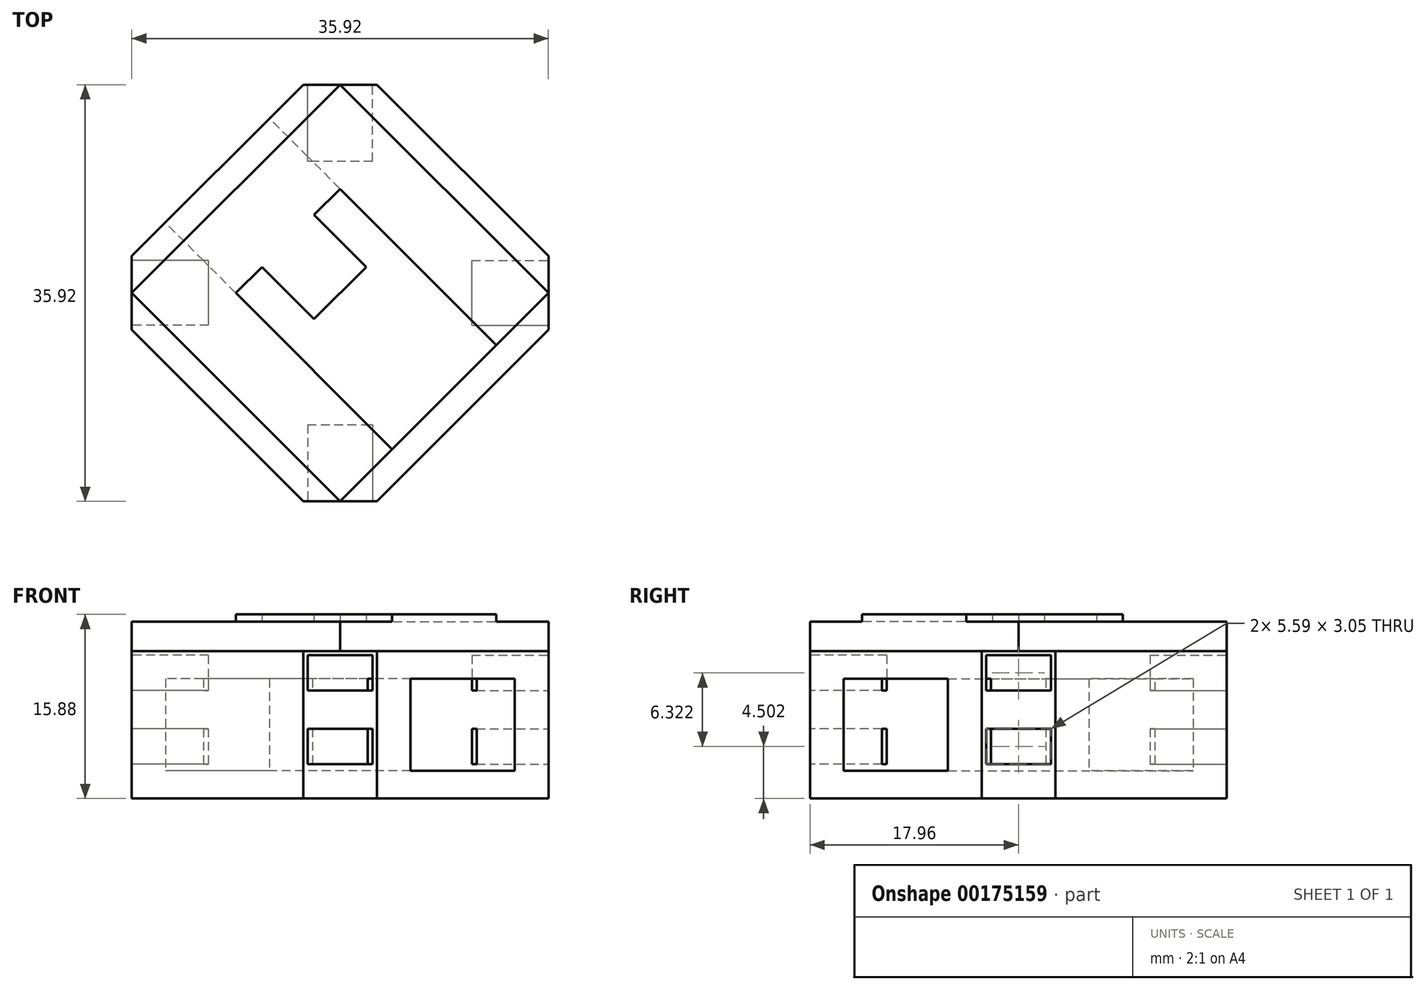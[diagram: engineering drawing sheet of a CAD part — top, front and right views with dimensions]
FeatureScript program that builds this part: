
annotation { "Feature Type Name" : "Feature", "Feature Type Description" : "" }
export const myFeature = defineFeature(function(context is Context, id is Id, definition is map)
    precondition{}
    {
        {
            var Q0;
            Q0=qCreatedBy(makeId("Top.planeOp"),FACE);
            var sketch = newSketch(context, id + "F0", { "sketchPlane" : qUnion([Q0])});
            skLineSegment(sketch, "E0.bottom", {"start": v(-17.96, 17.96) * mm, "end": v(17.96, 17.96) * mm});
            skLineSegment(sketch, "E0.top", {"start": v(-17.96, -17.96) * mm, "end": v(17.96, -17.96) * mm});
            skLineSegment(sketch, "E0.left", {"start": v(-17.96, 17.96) * mm, "end": v(-17.96, -17.96) * mm});
            skLineSegment(sketch, "E0.right", {"start": v(17.96, 17.96) * mm, "end": v(17.96, -17.96) * mm});
            skPoint(sketch, "E0.middle", {"position": v(0, 0) * mm});
            skPoint(sketch, "E1", {"position": v(-17.96, 3.17) * mm});
            skPoint(sketch, "E2", {"position": v(-17.96, -3.18) * mm});
            skPoint(sketch, "E3", {"position": v(-17.96, 0) * mm});
            skPoint(sketch, "E4", {"position": v(0, 17.96) * mm});
            skPoint(sketch, "E5", {"position": v(-3.17, 17.96) * mm});
            skPoint(sketch, "E6", {"position": v(3.18, 17.96) * mm});
            skPoint(sketch, "E7", {"position": v(17.96, 0) * mm});
            skPoint(sketch, "E8", {"position": v(17.96, 3.17) * mm});
            skPoint(sketch, "E9", {"position": v(17.96, -3.18) * mm});
            skPoint(sketch, "E10", {"position": v(0, -17.96) * mm});
            skPoint(sketch, "E11", {"position": v(3.18, -17.96) * mm});
            skPoint(sketch, "E12", {"position": v(-3.17, -17.96) * mm});
            skLineSegment(sketch, "E13", {"start": v(-17.96, 3.17) * mm, "end": v(-3.17, 17.96) * mm});
            skLineSegment(sketch, "E14", {"start": v(3.18, 17.96) * mm, "end": v(17.96, 3.17) * mm});
            skLineSegment(sketch, "E15", {"start": v(17.96, -3.18) * mm, "end": v(3.18, -17.96) * mm});
            skLineSegment(sketch, "E16", {"start": v(-17.96, -3.18) * mm, "end": v(-3.17, -17.96) * mm});
            skLineSegment(sketch, "E17", {"start": v(0, 0) * mm, "end": v(-8.98, 8.98) * mm});
            skLineSegment(sketch, "E18", {"start": v(0, 0) * mm, "end": v(8.98, 8.98) * mm});
            skLineSegment(sketch, "E19", {"start": v(0, 0) * mm, "end": v(8.98, -8.98) * mm});
            skLineSegment(sketch, "E20", {"start": v(0, 0) * mm, "end": v(-8.98, -8.98) * mm});
            skLineSegment(sketch, "E21", {"start": v(-8.98, -8.98) * mm, "end": v(0, -17.96) * mm});
            skLineSegment(sketch, "E22", {"start": v(0, -17.96) * mm, "end": v(8.98, -8.98) * mm});
            skLineSegment(sketch, "E23", {"start": v(-8.98, 8.98) * mm, "end": v(-17.96, 0) * mm});
            skLineSegment(sketch, "E24", {"start": v(-17.96, 0) * mm, "end": v(-8.98, -8.98) * mm});
            skLineSegment(sketch, "E25", {"start": v(-8.98, 8.98) * mm, "end": v(0, 17.96) * mm});
            skLineSegment(sketch, "E26", {"start": v(0, 17.96) * mm, "end": v(8.98, 8.98) * mm});
            skLineSegment(sketch, "E27", {"start": v(8.98, 8.98) * mm, "end": v(17.96, 0) * mm});
            skLineSegment(sketch, "E28", {"start": v(17.96, 0) * mm, "end": v(8.98, -8.98) * mm});
            skSolve(sketch);
        }
        {
            var Q0;
            Q0=makeQuery(id+"F0.imprint","IMPRINT",FACE,{"disambiguationData":[TD([[makeQuery(id+"F0.imprint","IMPRINT",EDGE,{"derivedFrom":sQuery(id+"F0.wireOp",EDGE,"E17")}),-1.0]])]});
            var Q1;
            Q1=makeQuery(id+"F0.imprint","IMPRINT",FACE,{"disambiguationData":[TD([[makeQuery(id+"F0.imprint","IMPRINT",EDGE,{"derivedFrom":sQuery(id+"F0.wireOp",EDGE,"E18")}),-1.0]])]});
            var Q2;
            Q2=makeQuery(id+"F0.imprint","IMPRINT",FACE,{"disambiguationData":[TD([[makeQuery(id+"F0.imprint","IMPRINT",EDGE,{"derivedFrom":sQuery(id+"F0.wireOp",EDGE,"E19")}),-1.0]])]});
            var Q3;
            Q3=makeQuery(id+"F0.imprint","IMPRINT",FACE,{"disambiguationData":[TD([[makeQuery(id+"F0.imprint","IMPRINT",EDGE,{"derivedFrom":sQuery(id+"F0.wireOp",EDGE,"E17")}),1.0]])]});
            extrude(context, id + "F1", {"entities" : qUnion([Q0, Q1, Q2, Q3]), "depth" : 15.24 * mm});
        }
        {
            var Q0;
            {var subQ1=sQuery(id+"F0.wireOp",EDGE,"E13");Q0=makeQuery(id+"F0.imprint","IMPRINT",FACE,{"disambiguationData":[TD([[makeQuery(id+"F0.imprint","IMPRINT",EDGE,{"derivedFrom":subQ1}),-1.0]])]});}
            var Q1;
            {var subQ1=sQuery(id+"F0.wireOp",EDGE,"E16");Q1=makeQuery(id+"F0.imprint","IMPRINT",FACE,{"disambiguationData":[TD([[makeQuery(id+"F0.imprint","IMPRINT",EDGE,{"derivedFrom":subQ1}),1.0]])]});}
            var Q2;
            {var subQ1=sQuery(id+"F0.wireOp",EDGE,"E15");Q2=makeQuery(id+"F0.imprint","IMPRINT",FACE,{"disambiguationData":[TD([[makeQuery(id+"F0.imprint","IMPRINT",EDGE,{"derivedFrom":subQ1}),-1.0]])]});}
            var Q3;
            {var subQ1=sQuery(id+"F0.wireOp",EDGE,"E14");Q3=makeQuery(id+"F0.imprint","IMPRINT",FACE,{"disambiguationData":[TD([[makeQuery(id+"F0.imprint","IMPRINT",EDGE,{"derivedFrom":subQ1}),-1.0]])]});}
            extrude(context, id + "F2", {"entities" : qUnion([Q0, Q1, Q2, Q3]), "operationType" : NewBodyOperationType.ADD, "depth" : 12.7 * mm});
        }
        {
            var Q0;
            Q0=makeQuery(id+"F2.opExtrude","CAP_FACE",FACE,{"disambiguationData":[OSD([sQuery(id+"F0.wireOp",EDGE,"E21"),sQuery(id+"F0.wireOp",EDGE,"E22"),sQuery(id+"F0.wireOp",EDGE,"E23"),sQuery(id+"F0.wireOp",EDGE,"E24"),sQuery(id+"F0.wireOp",EDGE,"E25"),sQuery(id+"F0.wireOp",EDGE,"E26"),sQuery(id+"F0.wireOp",EDGE,"E27"),sQuery(id+"F0.wireOp",EDGE,"E28")])],"isStart":false});
            var sketch = newSketch(context, id + "F3", { "sketchPlane" : qUnion([Q0])});
            skPoint(sketch, "E29", {"position": v(8.98, -8.98) * mm});
            skLineSegment(sketch, "E30", {"start": v(8.98, -8.98) * mm, "end": v(13.47, -4.5) * mm});
            skLineSegment(sketch, "E31", {"start": v(13.47, -4.5) * mm, "end": v(0, 8.98) * mm});
            skLineSegment(sketch, "E32", {"start": v(0, 8.98) * mm, "end": v(-2.25, 6.74) * mm});
            skLineSegment(sketch, "E33", {"start": v(-2.25, 6.74) * mm, "end": v(2.25, 2.25) * mm});
            skLineSegment(sketch, "E34", {"start": v(8.98, -8.98) * mm, "end": v(0, 0) * mm});
            skLineSegment(sketch, "E35", {"start": v(0, 0) * mm, "end": v(2.25, 2.25) * mm});
            skLineSegment(sketch, "E36.MirrorCS", {"start": v(0, 0) * mm, "end": v(-2.25, -2.25) * mm});
            skLineSegment(sketch, "E37.MirrorCS", {"start": v(-6.74, 2.25) * mm, "end": v(-2.25, -2.25) * mm});
            skLineSegment(sketch, "E38.MirrorCS", {"start": v(-8.98, 0) * mm, "end": v(-6.74, 2.25) * mm});
            skLineSegment(sketch, "E39.MirrorCS", {"start": v(4.5, -13.47) * mm, "end": v(-8.98, 0) * mm});
            skLineSegment(sketch, "E40.MirrorCS", {"start": v(8.98, -8.98) * mm, "end": v(4.5, -13.47) * mm});
            skSolve(sketch);
        }
        {
            var Q0;
            {var subQ0=sQuery(id+"F0.wireOp",EDGE,"E0.left");Q0=makeQuery(id+"F2.boolean.opBoolean","MERGE",FACE,{"derivedFrom":[makeQuery(id+"F2.opExtrude","SWEPT_FACE",FACE,{"disambiguationData":[OSD([subQ0]),TDD([makeQuery(id+"F0.imprint","IMPRINT",EDGE,{"disambiguationData":[TD([[makeQuery(id+"F0.imprint","INTERSECT",VERTEX,{"derivedFrom":[subQ0,sQuery(id+"F0.wireOp",EDGE,"E13")]}),-1.0]])],"derivedFrom":subQ0})])]}),makeQuery(id+"F2.opExtrude","SWEPT_FACE",FACE,{"disambiguationData":[OSD([subQ0]),TDD([makeQuery(id+"F0.imprint","IMPRINT",EDGE,{"disambiguationData":[TD([[makeQuery(id+"F0.imprint","INTERSECT",VERTEX,{"derivedFrom":[subQ0,sQuery(id+"F0.wireOp",EDGE,"E16")]}),1.0]])],"derivedFrom":subQ0})])]})]});}
            var sketch = newSketch(context, id + "F4", { "sketchPlane" : qUnion([Q0])});
            skPoint(sketch, "E41", {"position": v(0, 7.62) * mm});
            skPoint(sketch, "E42.positionSnap0", {"position": v(0, 5.33) * mm});
            skPoint(sketch, "E42.positionSnap1", {"position": v(3.3, 7.62) * mm});
            skLineSegment(sketch, "E43.bottom", {"start": v(-2.54, 12.07) * mm, "end": v(2.54, 12.07) * mm});
            skLineSegment(sketch, "E43.top", {"start": v(-2.54, 3.17) * mm, "end": v(2.54, 3.17) * mm});
            skLineSegment(sketch, "E44", {"start": v(-2.54, 9.58) * mm, "end": v(2.54, 9.58) * mm});
            skLineSegment(sketch, "E45", {"start": v(-2.54, 5.83) * mm, "end": v(2.54, 5.83) * mm});
            skLineSegment(sketch, "E46", {"start": v(-2.54, 12.07) * mm, "end": v(-2.54, 9.58) * mm});
            skLineSegment(sketch, "E47", {"start": v(2.54, 12.07) * mm, "end": v(2.54, 9.58) * mm});
            skLineSegment(sketch, "E48", {"start": v(-2.54, 5.83) * mm, "end": v(-2.54, 3.17) * mm});
            skLineSegment(sketch, "E49", {"start": v(2.54, 5.83) * mm, "end": v(2.54, 3.17) * mm});
            skPoint(sketch, "E50", {"position": v(0, 10.82) * mm});
            skPoint(sketch, "E50.positionSnap0", {"position": v(-2.54, 10.82) * mm});
            skPoint(sketch, "E50.positionSnap1", {"position": v(0, 9.58) * mm});
            skPoint(sketch, "E51", {"position": v(0, 4.5) * mm});
            skPoint(sketch, "E51.positionSnap0", {"position": v(-2.54, 4.5) * mm});
            skPoint(sketch, "E51.positionSnap1", {"position": v(0, 3.17) * mm});
            skLineSegment(sketch, "E52.bottom", {"start": v(-2.8, 6.03) * mm, "end": v(2.8, 6.03) * mm});
            skLineSegment(sketch, "E52.top", {"start": v(-2.8, 2.98) * mm, "end": v(2.8, 2.98) * mm});
            skLineSegment(sketch, "E52.left", {"start": v(-2.8, 6.03) * mm, "end": v(-2.8, 2.98) * mm});
            skLineSegment(sketch, "E52.right", {"start": v(2.8, 6.03) * mm, "end": v(2.8, 2.98) * mm});
            skLineSegment(sketch, "E53.bottom", {"start": v(-2.8, 12.35) * mm, "end": v(2.8, 12.35) * mm});
            skLineSegment(sketch, "E53.top", {"start": v(-2.8, 9.3) * mm, "end": v(2.8, 9.3) * mm});
            skLineSegment(sketch, "E53.left", {"start": v(-2.8, 12.35) * mm, "end": v(-2.8, 9.3) * mm});
            skLineSegment(sketch, "E53.right", {"start": v(2.8, 12.35) * mm, "end": v(2.8, 9.3) * mm});
            skLineSegment(sketch, "E54", {"start": v(0, 7.62) * mm, "end": v(0, 0) * mm});
            skSolve(sketch);
        }
        {
            var Q0;
            Q0=makeQuery(id+"F4.imprint","IMPRINT",FACE,{"disambiguationData":[TD([[makeQuery(id+"F4.imprint","IMPRINT",EDGE,{"derivedFrom":sQuery(id+"F4.wireOp",EDGE,"E43.bottom")}),1.0]])]});
            var Q1;
            Q1=makeQuery(id+"F4.imprint","IMPRINT",FACE,{"disambiguationData":[TD([[makeQuery(id+"F4.imprint","IMPRINT",EDGE,{"derivedFrom":sQuery(id+"F4.wireOp",EDGE,"E43.bottom")}),-1.0]])]});
            var Q2;
            Q2=makeQuery(id+"F4.imprint","IMPRINT",FACE,{"disambiguationData":[TD([[makeQuery(id+"F4.imprint","IMPRINT",EDGE,{"derivedFrom":sQuery(id+"F4.wireOp",EDGE,"E43.top")}),1.0]])]});
            var Q3;
            {var subQ4=sQuery(id+"F4.wireOp",EDGE,"E48");Q3=makeQuery(id+"F4.imprint","IMPRINT",FACE,{"disambiguationData":[TD([[makeQuery(id+"F4.imprint","IMPRINT",EDGE,{"derivedFrom":subQ4}),-1.0]])]});}
            var Q4;
            {var subQ8=sQuery(id+"F4.wireOp",EDGE,"E49");Q4=makeQuery(id+"F4.imprint","IMPRINT",FACE,{"disambiguationData":[TD([[makeQuery(id+"F4.imprint","IMPRINT",EDGE,{"derivedFrom":subQ8}),1.0]])]});}
            extrude(context, id + "F5", {"entities" : qUnion([Q0, Q1, Q2, Q3, Q4]), "operationType" : NewBodyOperationType.REMOVE, "oppositeDirection" : true, "depth" : 6.6 * mm});
        }
        {
            var Q0;
            {var subQ0=sQuery(id+"F0.wireOp",EDGE,"E0.right");Q0=makeQuery(id+"F2.boolean.opBoolean","MERGE",FACE,{"derivedFrom":[makeQuery(id+"F2.opExtrude","SWEPT_FACE",FACE,{"disambiguationData":[OSD([subQ0]),TDD([makeQuery(id+"F0.imprint","IMPRINT",EDGE,{"disambiguationData":[TD([[makeQuery(id+"F0.imprint","INTERSECT",VERTEX,{"derivedFrom":[subQ0,sQuery(id+"F0.wireOp",EDGE,"E14")]}),-1.0]])],"derivedFrom":subQ0})])]}),makeQuery(id+"F2.opExtrude","SWEPT_FACE",FACE,{"disambiguationData":[OSD([subQ0]),TDD([makeQuery(id+"F0.imprint","IMPRINT",EDGE,{"disambiguationData":[TD([[makeQuery(id+"F0.imprint","INTERSECT",VERTEX,{"derivedFrom":[subQ0,sQuery(id+"F0.wireOp",EDGE,"E15")]}),1.0]])],"derivedFrom":subQ0})])]})]});}
            var sketch = newSketch(context, id + "F6", { "sketchPlane" : qUnion([Q0])});
            skPoint(sketch, "E55", {"position": v(0, 7.62) * mm});
            skPoint(sketch, "E56.positionSnap0", {"position": v(0, 4.31) * mm});
            skPoint(sketch, "E56.positionSnap1", {"position": v(3.3, 7.62) * mm});
            skLineSegment(sketch, "E57.bottom", {"start": v(-2.54, 12.07) * mm, "end": v(2.54, 12.07) * mm});
            skLineSegment(sketch, "E57.top", {"start": v(-2.54, 3.18) * mm, "end": v(2.54, 3.18) * mm});
            skLineSegment(sketch, "E58", {"start": v(-2.54, 9.58) * mm, "end": v(2.54, 9.58) * mm});
            skLineSegment(sketch, "E59", {"start": v(-2.54, 5.83) * mm, "end": v(2.54, 5.83) * mm});
            skLineSegment(sketch, "E60", {"start": v(-2.54, 12.07) * mm, "end": v(-2.54, 9.58) * mm});
            skLineSegment(sketch, "E61", {"start": v(2.54, 12.07) * mm, "end": v(2.54, 9.58) * mm});
            skLineSegment(sketch, "E62", {"start": v(-2.54, 5.83) * mm, "end": v(-2.54, 3.18) * mm});
            skLineSegment(sketch, "E63", {"start": v(2.54, 5.83) * mm, "end": v(2.54, 3.18) * mm});
            skPoint(sketch, "E64", {"position": v(0, 10.82) * mm});
            skPoint(sketch, "E64.positionSnap0", {"position": v(-2.54, 10.82) * mm});
            skPoint(sketch, "E64.positionSnap1", {"position": v(0, 9.58) * mm});
            skPoint(sketch, "E65", {"position": v(0, 4.5) * mm});
            skPoint(sketch, "E65.positionSnap0", {"position": v(-2.54, 4.5) * mm});
            skPoint(sketch, "E65.positionSnap1", {"position": v(0, 3.18) * mm});
            skLineSegment(sketch, "E66.bottom", {"start": v(-2.8, 6.03) * mm, "end": v(2.8, 6.03) * mm});
            skLineSegment(sketch, "E66.top", {"start": v(-2.8, 2.98) * mm, "end": v(2.8, 2.98) * mm});
            skLineSegment(sketch, "E66.left", {"start": v(-2.8, 6.03) * mm, "end": v(-2.8, 2.98) * mm});
            skLineSegment(sketch, "E66.right", {"start": v(2.8, 6.03) * mm, "end": v(2.8, 2.98) * mm});
            skLineSegment(sketch, "E67.bottom", {"start": v(-2.8, 12.35) * mm, "end": v(2.8, 12.35) * mm});
            skLineSegment(sketch, "E67.top", {"start": v(-2.8, 9.3) * mm, "end": v(2.8, 9.3) * mm});
            skLineSegment(sketch, "E67.left", {"start": v(-2.8, 12.35) * mm, "end": v(-2.8, 9.3) * mm});
            skLineSegment(sketch, "E67.right", {"start": v(2.8, 12.35) * mm, "end": v(2.8, 9.3) * mm});
            skLineSegment(sketch, "E68", {"start": v(0, 7.62) * mm, "end": v(0, 0) * mm});
            skSolve(sketch);
        }
        {
            var Q0;
            Q0=makeQuery(id+"F6.imprint","IMPRINT",FACE,{"disambiguationData":[TD([[makeQuery(id+"F6.imprint","IMPRINT",EDGE,{"derivedFrom":sQuery(id+"F6.wireOp",EDGE,"E57.bottom")}),-1.0]])]});
            var Q1;
            {var subQ0=sQuery(id+"F6.wireOp",EDGE,"E63");Q1=makeQuery(id+"F6.imprint","IMPRINT",FACE,{"disambiguationData":[TD([[makeQuery(id+"F6.imprint","IMPRINT",EDGE,{"derivedFrom":subQ0}),-1.0]])]});}
            var Q2;
            {var subQ0=sQuery(id+"F6.wireOp",EDGE,"E62");Q2=makeQuery(id+"F6.imprint","IMPRINT",FACE,{"disambiguationData":[TD([[makeQuery(id+"F6.imprint","IMPRINT",EDGE,{"derivedFrom":subQ0}),1.0]])]});}
            var Q3;
            {var subQ4=sQuery(id+"F6.wireOp",EDGE,"E62");Q3=makeQuery(id+"F6.imprint","IMPRINT",FACE,{"disambiguationData":[TD([[makeQuery(id+"F6.imprint","IMPRINT",EDGE,{"derivedFrom":subQ4}),-1.0]])]});}
            var Q4;
            {var subQ4=sQuery(id+"F6.wireOp",EDGE,"E63");Q4=makeQuery(id+"F6.imprint","IMPRINT",FACE,{"disambiguationData":[TD([[makeQuery(id+"F6.imprint","IMPRINT",EDGE,{"derivedFrom":subQ4}),1.0]])]});}
            var Q5;
            Q5=makeQuery(id+"F6.imprint","IMPRINT",FACE,{"disambiguationData":[TD([[makeQuery(id+"F6.imprint","IMPRINT",EDGE,{"derivedFrom":sQuery(id+"F6.wireOp",EDGE,"E57.bottom")}),1.0]])]});
            extrude(context, id + "F7", {"entities" : qUnion([Q0, Q1, Q2, Q3, Q4, Q5]), "operationType" : NewBodyOperationType.REMOVE, "oppositeDirection" : true, "depth" : 6.6 * mm});
        }
        {
            var Q0;
            {var subQ0=sQuery(id+"F0.wireOp",EDGE,"E0.top");Q0=makeQuery(id+"F2.boolean.opBoolean","MERGE",FACE,{"derivedFrom":[makeQuery(id+"F2.opExtrude","SWEPT_FACE",FACE,{"disambiguationData":[OSD([subQ0]),TDD([makeQuery(id+"F0.imprint","IMPRINT",EDGE,{"disambiguationData":[TD([[makeQuery(id+"F0.imprint","INTERSECT",VERTEX,{"derivedFrom":[subQ0,sQuery(id+"F0.wireOp",EDGE,"E16")]}),-1.0]])],"derivedFrom":subQ0})])]}),makeQuery(id+"F2.opExtrude","SWEPT_FACE",FACE,{"disambiguationData":[OSD([subQ0]),TDD([makeQuery(id+"F0.imprint","IMPRINT",EDGE,{"disambiguationData":[TD([[makeQuery(id+"F0.imprint","INTERSECT",VERTEX,{"derivedFrom":[subQ0,sQuery(id+"F0.wireOp",EDGE,"E15")]}),1.0]])],"derivedFrom":subQ0})])]})]});}
            var sketch = newSketch(context, id + "F8", { "sketchPlane" : qUnion([Q0])});
            skPoint(sketch, "E69", {"position": v(0, 7.62) * mm});
            skPoint(sketch, "E69.positionSnap0", {"position": v(-25.4, 7.62) * mm});
            skPoint(sketch, "E70.positionSnap0", {"position": v(0, 5.76) * mm});
            skPoint(sketch, "E70.positionSnap1", {"position": v(3.3, 7.62) * mm});
            skLineSegment(sketch, "E71.bottom", {"start": v(-2.54, 12.07) * mm, "end": v(2.54, 12.07) * mm});
            skLineSegment(sketch, "E71.top", {"start": v(-2.54, 3.17) * mm, "end": v(2.54, 3.17) * mm});
            skLineSegment(sketch, "E72", {"start": v(-2.54, 9.58) * mm, "end": v(2.54, 9.58) * mm});
            skLineSegment(sketch, "E73", {"start": v(-2.54, 5.83) * mm, "end": v(2.54, 5.83) * mm});
            skLineSegment(sketch, "E74", {"start": v(-2.54, 12.07) * mm, "end": v(-2.54, 9.58) * mm});
            skLineSegment(sketch, "E75", {"start": v(2.54, 12.07) * mm, "end": v(2.54, 9.58) * mm});
            skLineSegment(sketch, "E76", {"start": v(-2.54, 5.83) * mm, "end": v(-2.54, 3.17) * mm});
            skLineSegment(sketch, "E77", {"start": v(2.54, 5.83) * mm, "end": v(2.54, 3.17) * mm});
            skPoint(sketch, "E78", {"position": v(0, 10.82) * mm});
            skPoint(sketch, "E78.positionSnap0", {"position": v(-2.54, 10.82) * mm});
            skPoint(sketch, "E78.positionSnap1", {"position": v(0, 9.58) * mm});
            skPoint(sketch, "E79", {"position": v(0, 4.5) * mm});
            skPoint(sketch, "E79.positionSnap0", {"position": v(-2.54, 4.5) * mm});
            skPoint(sketch, "E79.positionSnap1", {"position": v(0, 3.17) * mm});
            skLineSegment(sketch, "E80.bottom", {"start": v(-2.8, 6.03) * mm, "end": v(2.8, 6.03) * mm});
            skLineSegment(sketch, "E80.top", {"start": v(-2.8, 2.98) * mm, "end": v(2.8, 2.98) * mm});
            skLineSegment(sketch, "E80.left", {"start": v(-2.8, 6.03) * mm, "end": v(-2.8, 2.98) * mm});
            skLineSegment(sketch, "E80.right", {"start": v(2.8, 6.03) * mm, "end": v(2.8, 2.98) * mm});
            skLineSegment(sketch, "E81.bottom", {"start": v(-2.8, 12.35) * mm, "end": v(2.8, 12.35) * mm});
            skLineSegment(sketch, "E81.top", {"start": v(-2.8, 9.3) * mm, "end": v(2.8, 9.3) * mm});
            skLineSegment(sketch, "E81.left", {"start": v(-2.8, 12.35) * mm, "end": v(-2.8, 9.3) * mm});
            skLineSegment(sketch, "E81.right", {"start": v(2.8, 12.35) * mm, "end": v(2.8, 9.3) * mm});
            skLineSegment(sketch, "E82", {"start": v(0, 7.62) * mm, "end": v(0, 0) * mm});
            skSolve(sketch);
        }
        {
            var Q0;
            Q0=makeQuery(id+"F8.imprint","IMPRINT",FACE,{"disambiguationData":[TD([[makeQuery(id+"F8.imprint","IMPRINT",EDGE,{"derivedFrom":sQuery(id+"F8.wireOp",EDGE,"E71.bottom")}),1.0]])]});
            var Q1;
            {var subQ4=sQuery(id+"F8.wireOp",EDGE,"E77");Q1=makeQuery(id+"F8.imprint","IMPRINT",FACE,{"disambiguationData":[TD([[makeQuery(id+"F8.imprint","IMPRINT",EDGE,{"derivedFrom":subQ4}),1.0]])]});}
            var Q2;
            {var subQ4=sQuery(id+"F8.wireOp",EDGE,"E76");Q2=makeQuery(id+"F8.imprint","IMPRINT",FACE,{"disambiguationData":[TD([[makeQuery(id+"F8.imprint","IMPRINT",EDGE,{"derivedFrom":subQ4}),-1.0]])]});}
            var Q3;
            {var subQ0=sQuery(id+"F8.wireOp",EDGE,"E76");Q3=makeQuery(id+"F8.imprint","IMPRINT",FACE,{"disambiguationData":[TD([[makeQuery(id+"F8.imprint","IMPRINT",EDGE,{"derivedFrom":subQ0}),1.0]])]});}
            var Q4;
            Q4=makeQuery(id+"F8.imprint","IMPRINT",FACE,{"disambiguationData":[TD([[makeQuery(id+"F8.imprint","IMPRINT",EDGE,{"derivedFrom":sQuery(id+"F8.wireOp",EDGE,"E71.bottom")}),-1.0]])]});
            var Q5;
            {var subQ0=sQuery(id+"F8.wireOp",EDGE,"E77");Q5=makeQuery(id+"F8.imprint","IMPRINT",FACE,{"disambiguationData":[TD([[makeQuery(id+"F8.imprint","IMPRINT",EDGE,{"derivedFrom":subQ0}),-1.0]])]});}
            extrude(context, id + "F9", {"entities" : qUnion([Q0, Q1, Q2, Q3, Q4, Q5]), "operationType" : NewBodyOperationType.REMOVE, "oppositeDirection" : true, "depth" : 6.6 * mm});
        }
        {
            var Q0;
            Q0 = qSketchRegion(id + "F3", true);
            extrude(context, id + "F10", {"entities" : qUnion([Q0]), "operationType" : NewBodyOperationType.ADD, "depth" : 3.17 * mm});
        }
        {
            var Q0;
            {var subQ0=sQuery(id+"F0.wireOp",EDGE,"E0.bottom");Q0=makeQuery(id+"F2.boolean.opBoolean","MERGE",FACE,{"derivedFrom":[makeQuery(id+"F2.opExtrude","SWEPT_FACE",FACE,{"disambiguationData":[OSD([subQ0]),TDD([makeQuery(id+"F0.imprint","IMPRINT",EDGE,{"disambiguationData":[TD([[makeQuery(id+"F0.imprint","INTERSECT",VERTEX,{"derivedFrom":[subQ0,sQuery(id+"F0.wireOp",EDGE,"E13")]}),-1.0]])],"derivedFrom":subQ0})])]}),makeQuery(id+"F2.opExtrude","SWEPT_FACE",FACE,{"disambiguationData":[OSD([subQ0]),TDD([makeQuery(id+"F0.imprint","IMPRINT",EDGE,{"disambiguationData":[TD([[makeQuery(id+"F0.imprint","INTERSECT",VERTEX,{"derivedFrom":[subQ0,sQuery(id+"F0.wireOp",EDGE,"E14")]}),1.0]])],"derivedFrom":subQ0})])]})]});}
            var sketch = newSketch(context, id + "F11", { "sketchPlane" : qUnion([Q0])});
            skPoint(sketch, "E83", {"position": v(0, 7.62) * mm});
            skPoint(sketch, "E84.positionSnap0", {"position": v(0, 4.31) * mm});
            skPoint(sketch, "E84.positionSnap1", {"position": v(3.3, 7.62) * mm});
            skLineSegment(sketch, "E85.bottom", {"start": v(-2.54, 12.07) * mm, "end": v(2.54, 12.07) * mm});
            skLineSegment(sketch, "E85.top", {"start": v(-2.54, 3.18) * mm, "end": v(2.54, 3.18) * mm});
            skLineSegment(sketch, "E86", {"start": v(-2.54, 9.58) * mm, "end": v(2.54, 9.58) * mm});
            skLineSegment(sketch, "E87", {"start": v(-2.54, 5.83) * mm, "end": v(2.54, 5.83) * mm});
            skLineSegment(sketch, "E88", {"start": v(-2.54, 12.07) * mm, "end": v(-2.54, 9.58) * mm});
            skLineSegment(sketch, "E89", {"start": v(2.54, 12.07) * mm, "end": v(2.54, 9.58) * mm});
            skLineSegment(sketch, "E90", {"start": v(-2.54, 5.83) * mm, "end": v(-2.54, 3.18) * mm});
            skLineSegment(sketch, "E91", {"start": v(2.54, 5.83) * mm, "end": v(2.54, 3.18) * mm});
            skPoint(sketch, "E92", {"position": v(0, 10.82) * mm});
            skPoint(sketch, "E92.positionSnap0", {"position": v(-2.54, 10.82) * mm});
            skPoint(sketch, "E92.positionSnap1", {"position": v(0, 9.58) * mm});
            skPoint(sketch, "E93", {"position": v(0, 4.5) * mm});
            skPoint(sketch, "E93.positionSnap0", {"position": v(-2.54, 4.5) * mm});
            skPoint(sketch, "E93.positionSnap1", {"position": v(0, 3.18) * mm});
            skLineSegment(sketch, "E94.bottom", {"start": v(-2.8, 6.03) * mm, "end": v(2.8, 6.03) * mm});
            skLineSegment(sketch, "E94.top", {"start": v(-2.8, 2.98) * mm, "end": v(2.8, 2.98) * mm});
            skLineSegment(sketch, "E94.left", {"start": v(-2.8, 6.03) * mm, "end": v(-2.8, 2.98) * mm});
            skLineSegment(sketch, "E94.right", {"start": v(2.8, 6.03) * mm, "end": v(2.8, 2.98) * mm});
            skLineSegment(sketch, "E95.bottom", {"start": v(-2.8, 12.35) * mm, "end": v(2.8, 12.35) * mm});
            skLineSegment(sketch, "E95.top", {"start": v(-2.8, 9.3) * mm, "end": v(2.8, 9.3) * mm});
            skLineSegment(sketch, "E95.left", {"start": v(-2.8, 12.35) * mm, "end": v(-2.8, 9.3) * mm});
            skLineSegment(sketch, "E95.right", {"start": v(2.8, 12.35) * mm, "end": v(2.8, 9.3) * mm});
            skLineSegment(sketch, "E96", {"start": v(0, 7.62) * mm, "end": v(0, 0) * mm});
            skSolve(sketch);
        }
        {
            var Q0;
            Q0 = qSketchRegion(id + "F11", true);
            var Q1;
            {var subQ0=sQuery(id+"F11.wireOp",EDGE,"E90");Q1=makeQuery(id+"F11.imprint","IMPRINT",FACE,{"disambiguationData":[TD([[makeQuery(id+"F11.imprint","IMPRINT",EDGE,{"derivedFrom":subQ0}),1.0]])]});}
            var Q2;
            {var subQ0=sQuery(id+"F11.wireOp",EDGE,"E91");Q2=makeQuery(id+"F11.imprint","IMPRINT",FACE,{"disambiguationData":[TD([[makeQuery(id+"F11.imprint","IMPRINT",EDGE,{"derivedFrom":subQ0}),-1.0]])]});}
            var Q3;
            Q3=makeQuery(id+"F11.imprint","IMPRINT",FACE,{"disambiguationData":[TD([[makeQuery(id+"F11.imprint","IMPRINT",EDGE,{"derivedFrom":sQuery(id+"F11.wireOp",EDGE,"E85.bottom")}),-1.0]])]});
            extrude(context, id + "F12", {"entities" : qUnion([Q0, Q1, Q2, Q3]), "operationType" : NewBodyOperationType.REMOVE, "oppositeDirection" : true, "depth" : 6.6 * mm});
        }
        {
            var Q0;
            Q0=makeQuery(id+"F2.opExtrude","SWEPT_FACE",FACE,{"disambiguationData":[OSD([sQuery(id+"F0.wireOp",EDGE,"E13")])]});
            var sketch = newSketch(context, id + "F13", { "sketchPlane" : qUnion([Q0])});
            skLineSegment(sketch, "E97", {"start": v(0, 0) * mm, "end": v(0, 6.35) * mm});
            skPoint(sketch, "E97.endSnap0", {"position": v(0, 12.7) * mm});
            skLineSegment(sketch, "E98.bottom", {"start": v(-6.35, 10.32) * mm, "end": v(6.35, 10.32) * mm});
            skLineSegment(sketch, "E98.top", {"start": v(-6.35, 2.38) * mm, "end": v(6.35, 2.38) * mm});
            skLineSegment(sketch, "E98.left", {"start": v(-6.35, 10.32) * mm, "end": v(-6.35, 2.38) * mm});
            skLineSegment(sketch, "E98.right", {"start": v(6.35, 10.32) * mm, "end": v(6.35, 2.38) * mm});
            skPoint(sketch, "E98.middle", {"position": v(0, 6.35) * mm});
            skSolve(sketch);
        }
        {
            var Q0;
            Q0=makeQuery(id+"F13.imprint","IMPRINT",FACE,{"disambiguationData":[TD([[makeQuery(id+"F13.imprint","IMPRINT",EDGE,{"derivedFrom":sQuery(id+"F13.wireOp",EDGE,"E98.bottom")}),-1.0]])]});
            extrude(context, id + "F14", {"entities" : qUnion([Q0]), "operationType" : NewBodyOperationType.REMOVE, "oppositeDirection" : true, "depth" : 38.1 * mm});
        }
    });
